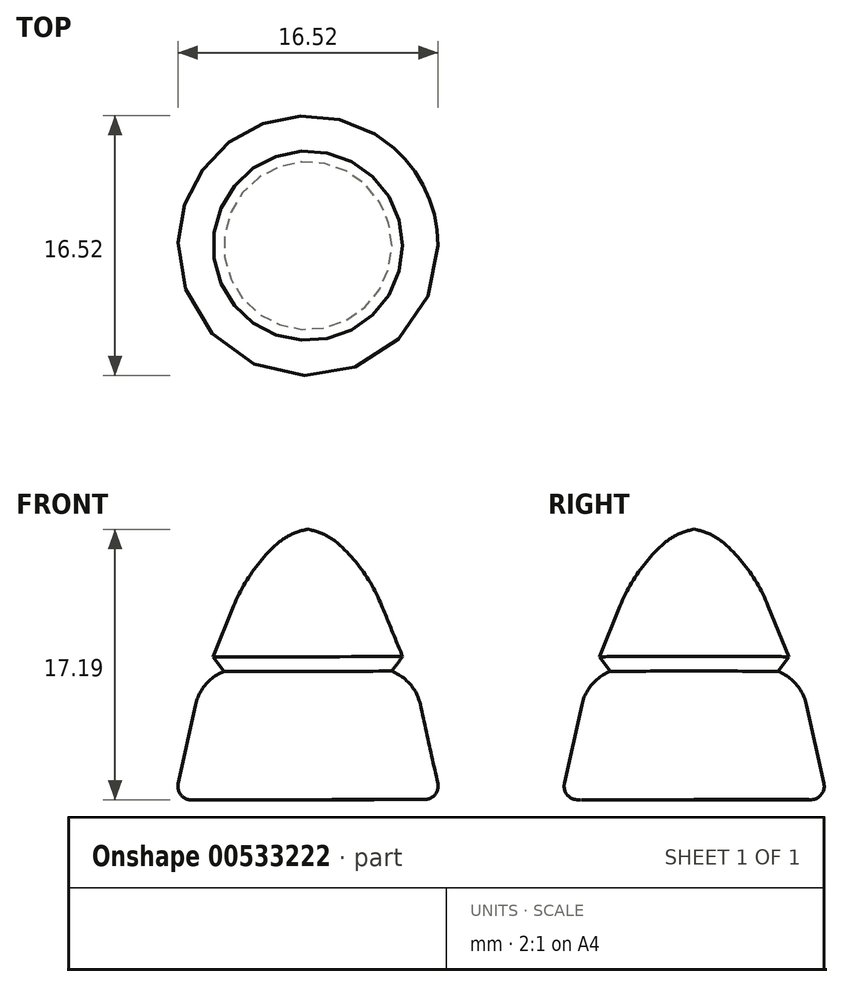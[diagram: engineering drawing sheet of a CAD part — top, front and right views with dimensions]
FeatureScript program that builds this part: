
annotation { "Feature Type Name" : "Feature", "Feature Type Description" : "" }
export const myFeature = defineFeature(function(context is Context, id is Id, definition is map)
    precondition{}
    {
        {
            var Q0;
            Q0=qCreatedBy(makeId("Front.planeOp"),FACE);
            var sketch = newSketch(context, id + "F0", { "sketchPlane" : qUnion([Q0])});
            skLineSegment(sketch, "E0", {"start": v(0, 0) * mm, "end": v(-8.47, 0) * mm});
            skLineSegment(sketch, "E1", {"start": v(-8.47, 0) * mm, "end": v(-6.78, 7.72) * mm});
            skLineSegment(sketch, "E2", {"start": v(-6.78, 7.72) * mm, "end": v(-5.34, 8.16) * mm});
            skLineSegment(sketch, "E3", {"start": v(-5.34, 8.16) * mm, "end": v(-6.03, 9.08) * mm});
            skLineSegment(sketch, "E4", {"start": v(-6.03, 9.08) * mm, "end": v(-3.72, 14.78) * mm});
            skLineSegment(sketch, "E5", {"start": v(-3.72, 14.78) * mm, "end": v(-1.2, 16.92) * mm});
            skLineSegment(sketch, "E6", {"start": v(-1.2, 16.92) * mm, "end": v(-0.03, 17.2) * mm});
            skLineSegment(sketch, "E7", {"start": v(-0.03, 17.2) * mm, "end": v(0, 0) * mm});
            skSolve(sketch);
        }
        {
            var Q0;
            Q0=makeQuery(id+"F0.imprint","IMPRINT",FACE,{"disambiguationData":[TD([[makeQuery(id+"F0.imprint","IMPRINT",EDGE,{"derivedFrom":sQuery(id+"F0.wireOp",EDGE,"E0")}),-1.0]])]});
            var Q1;
            Q1=sQuery(id+"F0.wireOp",EDGE,"E7");
            revolve(context, id + "F1", {"entities" : qUnion([Q0]), "axis" : qUnion([Q1]), "revolveType" : RevolveType.FULL});
        }
        {
            var Q0;
            Q0=makeQuery(id+"F1.opRevolve","SWEPT_EDGE",EDGE,{"disambiguationData":[OSD([sQuery(id+"F0.wireOp",EDGE,"E4"),sQuery(id+"F0.wireOp",EDGE,"E5")])]});
            fillet(context, id + "F2", {"entities" : qUnion([Q0]), "radius" : 10.83 * mm, "tangentPropagation" : true, "allowEdgeOverflow" : false});
        }
        {
            var Q0;
            Q0=makeQuery(id+"F1.opRevolve","SWEPT_EDGE",EDGE,{"disambiguationData":[OSD([sQuery(id+"F0.wireOp",EDGE,"E5"),sQuery(id+"F0.wireOp",EDGE,"E6")])]});
            fillet(context, id + "F3", {"entities" : qUnion([Q0]), "radius" : 4 * mm, "tangentPropagation" : true, "allowEdgeOverflow" : false});
        }
        {
            var Q0;
            Q0=makeQuery(id+"F1.opRevolve","SWEPT_EDGE",EDGE,{"disambiguationData":[OSD([sQuery(id+"F0.wireOp",EDGE,"E0"),sQuery(id+"F0.wireOp",EDGE,"E1")])]});
            fillet(context, id + "F4", {"entities" : qUnion([Q0]), "radius" : 0.84 * mm, "tangentPropagation" : true, "allowEdgeOverflow" : false});
        }
        {
            var Q0;
            Q0=makeQuery(id+"F1.opRevolve","SWEPT_EDGE",EDGE,{"disambiguationData":[OSD([sQuery(id+"F0.wireOp",EDGE,"E1"),sQuery(id+"F0.wireOp",EDGE,"E2")])]});
            fillet(context, id + "F5", {"entities" : qUnion([Q0]), "radius" : 2.97 * mm, "tangentPropagation" : true, "allowEdgeOverflow" : false});
        }
    });
